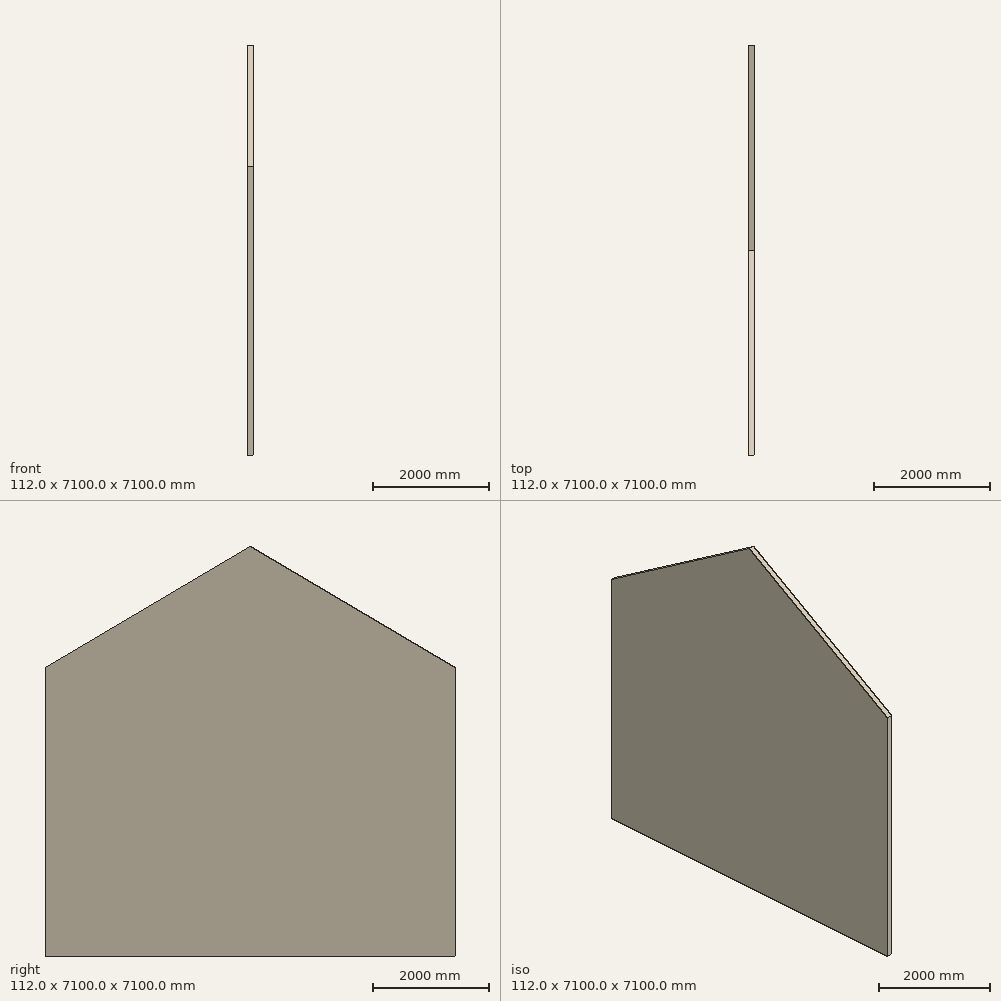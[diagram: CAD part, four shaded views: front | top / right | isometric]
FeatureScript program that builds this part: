
annotation { "Feature Type Name" : "Feature", "Feature Type Description" : "" }
export const myFeature = defineFeature(function(context is Context, id is Id, definition is map)
    precondition{}
    {
        {
            var Q0;
            Q0=qCreatedBy(makeId("Right.planeOp"),FACE);
            var sketch = newSketch(context, id + "F0", { "sketchPlane" : qUnion([Q0])});
            skLineSegment(sketch, "E0.bottom", {"start": v(3548.36, -2713.57) * mm, "end": v(-3551.64, -2713.57) * mm});
            skLineSegment(sketch, "E0.left", {"start": v(3548.36, -2713.57) * mm, "end": v(3548.36, 2286.43) * mm});
            skLineSegment(sketch, "E0.right", {"start": v(-3551.64, -2713.57) * mm, "end": v(-3551.64, 2286.43) * mm});
            skLineSegment(sketch, "E1", {"start": v(3548.36, 2286.43) * mm, "end": v(-1.64, 4386.43) * mm});
            skLineSegment(sketch, "E2", {"start": v(-3551.64, 2286.43) * mm, "end": v(-1.64, 4386.43) * mm});
            skSolve(sketch);
        }
        {
            var Q0;
            Q0=qSketchRegion(id+"F0",true);
            extrude(context, id + "F1", {"entities" : qUnion([Q0]), "depth" : 112 * mm, "offsetDistance" : 25 * mm});
        }
    });
